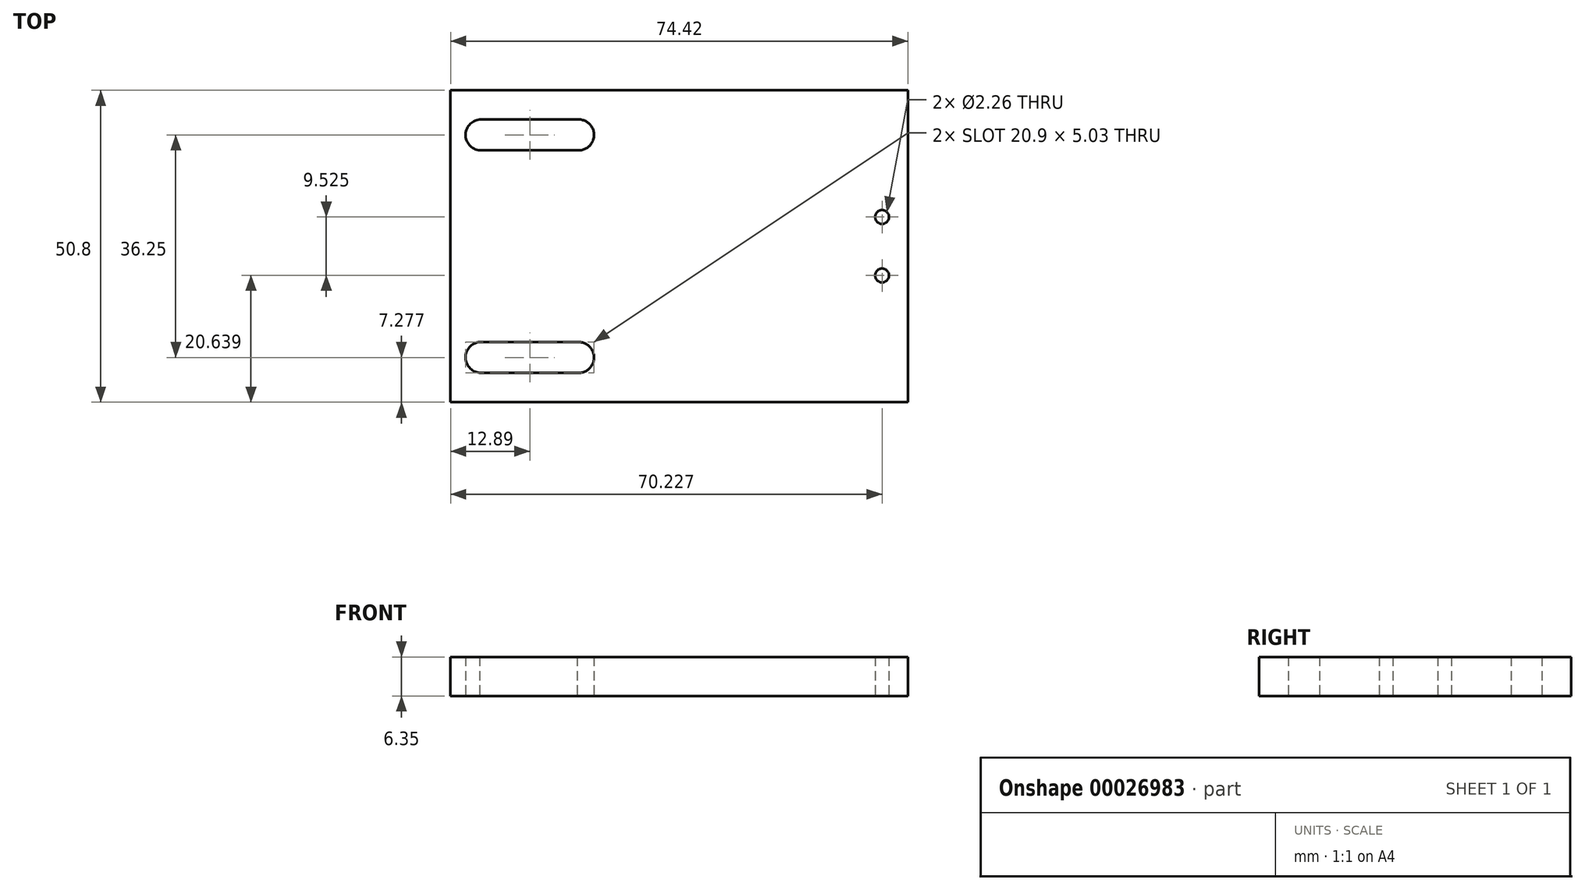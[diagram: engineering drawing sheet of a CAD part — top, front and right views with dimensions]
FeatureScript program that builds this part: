
annotation { "Feature Type Name" : "Feature", "Feature Type Description" : "" }
export const myFeature = defineFeature(function(context is Context, id is Id, definition is map)
    precondition{}
    {
        {
            var Q0;
            Q0=qCreatedBy(makeId("Top.planeOp"),FACE);
            var sketch = newSketch(context, id + "F0", { "sketchPlane" : qUnion([Q0])});
            skLineSegment(sketch, "E0.bottom", {"start": v(-42.43, 48.87) * mm, "end": v(31.99, 48.87) * mm});
            skLineSegment(sketch, "E0.top", {"start": v(-42.43, -1.93) * mm, "end": v(31.99, -1.93) * mm});
            skLineSegment(sketch, "E0.left", {"start": v(-42.43, 48.87) * mm, "end": v(-42.43, -1.93) * mm});
            skLineSegment(sketch, "E0.right", {"start": v(31.99, 48.87) * mm, "end": v(31.99, -1.93) * mm});
            skLineSegment(sketch, "E1", {"start": v(-37.48, 44.1) * mm, "end": v(-21.6, 44.1) * mm});
            skLineSegment(sketch, "E2", {"start": v(-37.67, 39.08) * mm, "end": v(-21.8, 39.08) * mm});
            skArc(sketch, "E3", {"start": v(-37.48, 44.1) * mm, "mid": v(-40, 41.7) * mm, "end": v(-37.67, 39.08) * mm});
            skArc(sketch, "E4", {"start": v(-21.6, 44.1) * mm, "mid": v(-19.09, 41.5) * mm, "end": v(-21.8, 39.08) * mm});
            skCircle(sketch, "E5", {"center": v(27.8, 28.23) * mm, "radius": 1.13 * mm});
            skCircle(sketch, "E6.MirrorC", {"center": v(27.8, 18.7) * mm, "radius": 1.13 * mm});
            skLineSegment(sketch, "E7.MirrorCS", {"start": v(-37.67, 7.86) * mm, "end": v(-21.8, 7.86) * mm});
            skLineSegment(sketch, "E8.MirrorCS", {"start": v(-37.48, 2.83) * mm, "end": v(-21.6, 2.83) * mm});
            skArc(sketch, "E9.MirrorCS", {"start": v(-37.48, 2.83) * mm, "mid": v(-40, 5.25) * mm, "end": v(-37.67, 7.86) * mm});
            skArc(sketch, "E10.MirrorCS", {"start": v(-21.6, 2.83) * mm, "mid": v(-19.09, 5.45) * mm, "end": v(-21.8, 7.86) * mm});
            skSolve(sketch);
        }
        {
            var Q0;
            Q0=makeQuery(id+"F0.imprint","IMPRINT",FACE,{"disambiguationData":[TD([[makeQuery(id+"F0.imprint","IMPRINT",EDGE,{"derivedFrom":sQuery(id+"F0.wireOp",EDGE,"E0.bottom")}),-1.0]])]});
            extrude(context, id + "F1", {"entities" : qUnion([Q0]), "depth" : 6.35 * mm});
        }
    });
